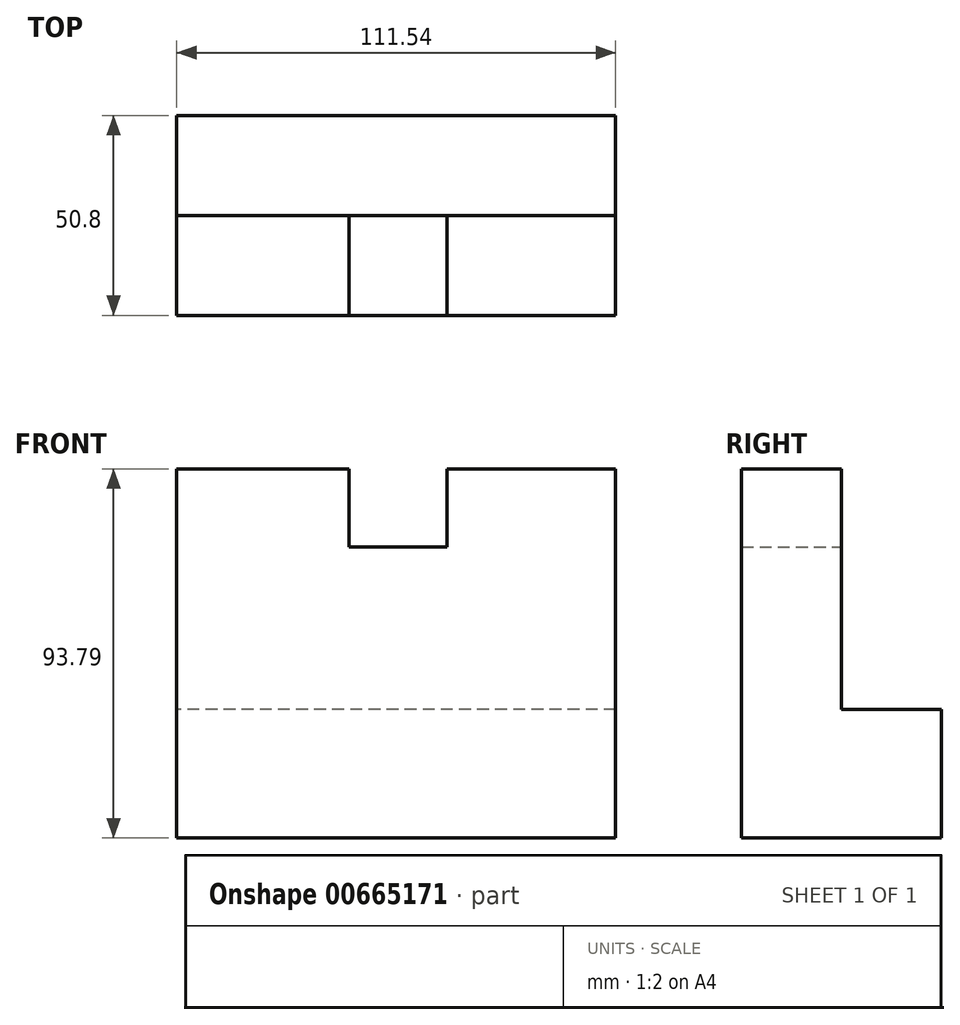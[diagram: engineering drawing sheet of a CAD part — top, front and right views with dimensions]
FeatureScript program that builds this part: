
annotation { "Feature Type Name" : "Feature", "Feature Type Description" : "" }
export const myFeature = defineFeature(function(context is Context, id is Id, definition is map)
    precondition{}
    {
        {
            var Q0;
            Q0=qCreatedBy(makeId("Front.planeOp"),FACE);
            var sketch = newSketch(context, id + "F0", { "sketchPlane" : qUnion([Q0])});
            skLineSegment(sketch, "E0", {"start": v(-54.9, 0) * mm, "end": v(-54.9, 61.1) * mm});
            skLineSegment(sketch, "E1", {"start": v(-54.9, 61.1) * mm, "end": v(-11.07, 61.1) * mm});
            skLineSegment(sketch, "E2", {"start": v(-11.07, 61.1) * mm, "end": v(-11.07, 41.31) * mm});
            skLineSegment(sketch, "E3", {"start": v(-11.07, 41.31) * mm, "end": v(13.81, 41.31) * mm});
            skLineSegment(sketch, "E4", {"start": v(13.81, 41.31) * mm, "end": v(13.81, 61.1) * mm});
            skLineSegment(sketch, "E5", {"start": v(13.81, 61.1) * mm, "end": v(56.63, 61.1) * mm});
            skLineSegment(sketch, "E6", {"start": v(56.63, 61.1) * mm, "end": v(56.63, -22.71) * mm});
            skLineSegment(sketch, "E7", {"start": v(56.63, -22.71) * mm, "end": v(56.63, -32.7) * mm});
            skLineSegment(sketch, "E8", {"start": v(56.63, -32.7) * mm, "end": v(-22.69, -32.7) * mm});
            skLineSegment(sketch, "E9", {"start": v(-22.69, -32.7) * mm, "end": v(-54.9, -32.7) * mm});
            skLineSegment(sketch, "E10", {"start": v(-54.9, -32.7) * mm, "end": v(-54.9, 0) * mm});
            skSolve(sketch);
        }
        {
            var Q0;
            Q0 = qSketchRegion(id + "F0", true);
            extrude(context, id + "F1", {"entities" : qUnion([Q0]), "depth" : 25.4 * mm, "offsetDistance" : 25.4 * mm});
        }
        {
            var Q0;
            Q0=makeQuery(id+"F1.opExtrude","CAP_FACE",FACE,{"disambiguationData":[OSD([sQuery(id+"F0.wireOp",EDGE,"E0"),sQuery(id+"F0.wireOp",EDGE,"E1"),sQuery(id+"F0.wireOp",EDGE,"E2"),sQuery(id+"F0.wireOp",EDGE,"E3"),sQuery(id+"F0.wireOp",EDGE,"E4"),sQuery(id+"F0.wireOp",EDGE,"E5"),sQuery(id+"F0.wireOp",EDGE,"E6"),sQuery(id+"F0.wireOp",EDGE,"E7"),sQuery(id+"F0.wireOp",EDGE,"E8"),sQuery(id+"F0.wireOp",EDGE,"E9"),sQuery(id+"F0.wireOp",EDGE,"E10")])],"isStart":true});
            var sketch = newSketch(context, id + "F2", { "sketchPlane" : qUnion([Q0])});
            skLineSegment(sketch, "E11.bottom", {"start": v(-56.63, -32.7) * mm, "end": v(54.9, -32.7) * mm});
            skLineSegment(sketch, "E11.top", {"start": v(-56.63, 0) * mm, "end": v(54.9, 0) * mm});
            skLineSegment(sketch, "E11.left", {"start": v(-56.63, -32.7) * mm, "end": v(-56.63, 0) * mm});
            skLineSegment(sketch, "E11.right", {"start": v(54.9, -32.7) * mm, "end": v(54.9, 0) * mm});
            skSolve(sketch);
        }
        {
            var Q0;
            Q0 = qSketchRegion(id + "F2", true);
            extrude(context, id + "F3", {"entities" : qUnion([Q0]), "operationType" : NewBodyOperationType.ADD, "depth" : 25.4 * mm, "offsetDistance" : 25.4 * mm});
        }
    });
